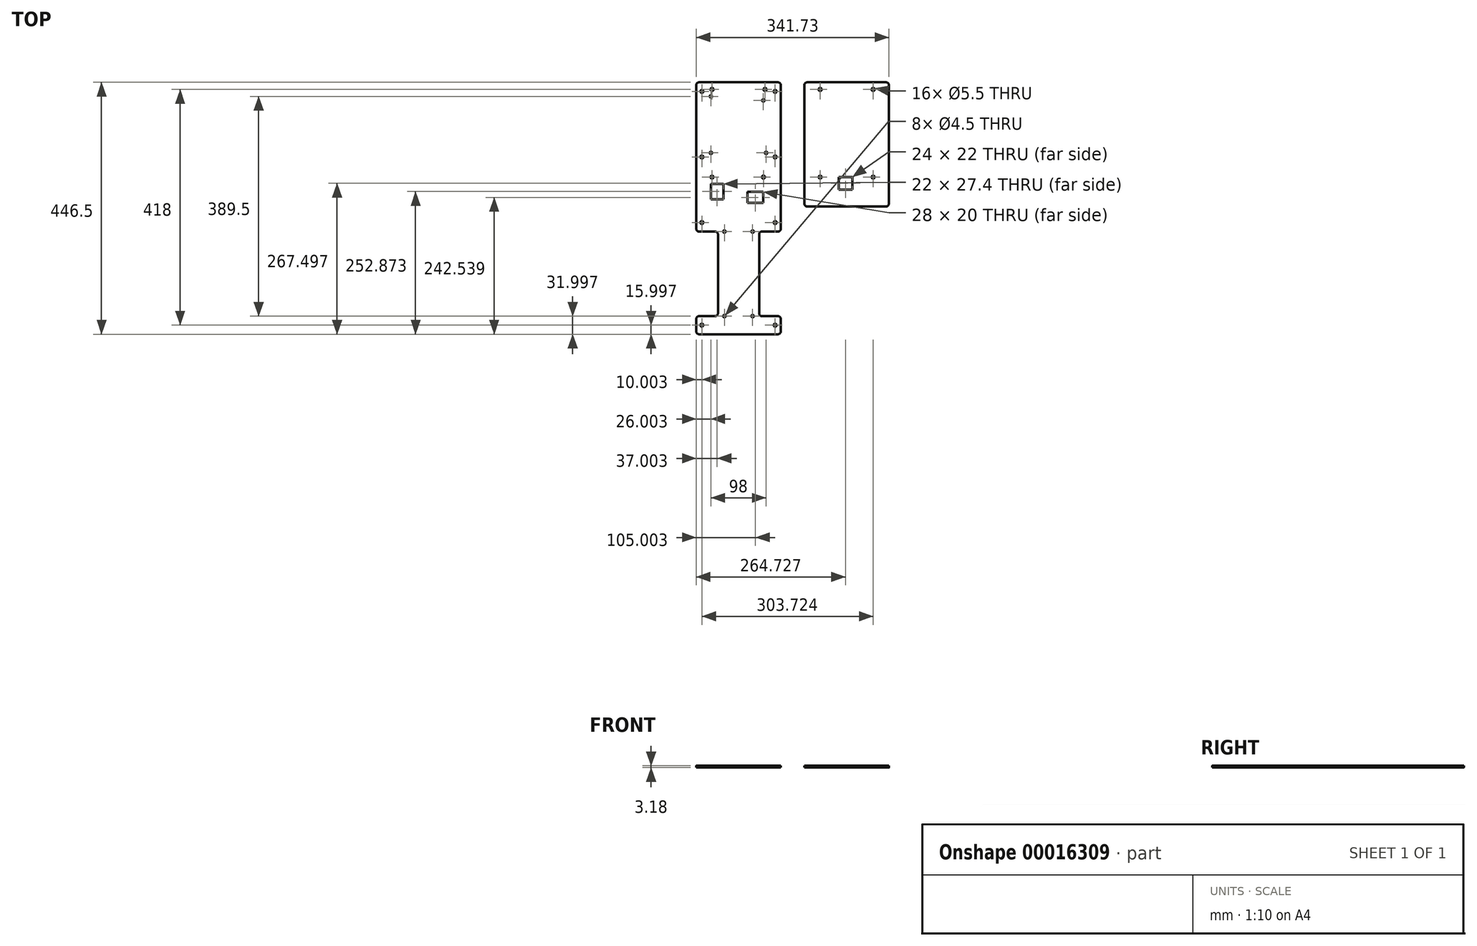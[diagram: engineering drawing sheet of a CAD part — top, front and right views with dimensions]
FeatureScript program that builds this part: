
annotation { "Feature Type Name" : "Feature", "Feature Type Description" : "" }
export const myFeature = defineFeature(function(context is Context, id is Id, definition is map)
    precondition{}
    {
        {
            var Q0;
            Q0=qCreatedBy(makeId("Top.planeOp"),FACE);
            var sketch = newSketch(context, id + "F0", { "sketchPlane" : qUnion([Q0])});
            skLineSegment(sketch, "E0.bottom", {"start": v(-64.08, 304.56) * mm, "end": v(75.92, 304.56) * mm});
            skLineSegment(sketch, "E0.top", {"start": v(-64.08, -141.94) * mm, "end": v(75.92, -141.94) * mm});
            skLineSegment(sketch, "E0.left", {"start": v(-69.08, 299.56) * mm, "end": v(-69.08, 45.06) * mm});
            skLineSegment(sketch, "E0.right", {"start": v(80.92, 299.56) * mm, "end": v(80.92, 45.06) * mm});
            skLineSegment(sketch, "E1.bottom", {"start": v(-64.08, 40.06) * mm, "end": v(-35.58, 40.06) * mm});
            skLineSegment(sketch, "E1.top", {"start": v(-64.08, -109.94) * mm, "end": v(-35.58, -109.94) * mm});
            skLineSegment(sketch, "E1.right", {"start": v(-30.58, 35.06) * mm, "end": v(-30.58, -104.94) * mm});
            skLineSegment(sketch, "E2.trimOffspring", {"start": v(-69.08, -114.94) * mm, "end": v(-69.08, -136.94) * mm});
            skLineSegment(sketch, "E3.bottom", {"start": v(75.92, 40.06) * mm, "end": v(47.42, 40.06) * mm});
            skLineSegment(sketch, "E3.top", {"start": v(75.92, -109.94) * mm, "end": v(47.42, -109.94) * mm});
            skLineSegment(sketch, "E3.right", {"start": v(42.42, 35.06) * mm, "end": v(42.42, -104.94) * mm});
            skLineSegment(sketch, "E4.trimOffspring", {"start": v(80.92, -114.94) * mm, "end": v(80.92, -136.94) * mm});
            skLineSegment(sketch, "E5", {"start": v(-69.08, -109.94) * mm, "end": v(-19.08, -109.94) * mm, "construction": true});
            skLineSegment(sketch, "E6", {"start": v(-19.08, -109.94) * mm, "end": v(30.92, -109.94) * mm, "construction": true});
            skLineSegment(sketch, "E7", {"start": v(30.92, -109.94) * mm, "end": v(80.92, -109.94) * mm, "construction": true});
            skLineSegment(sketch, "E8", {"start": v(-19.08, -109.94) * mm, "end": v(-19.08, -141.94) * mm, "construction": true});
            skLineSegment(sketch, "E9", {"start": v(-19.08, -109.94) * mm, "end": v(-19.08, 40.06) * mm, "construction": true});
            skLineSegment(sketch, "E10", {"start": v(-19.08, 40.06) * mm, "end": v(30.92, 40.06) * mm, "construction": true});
            skLineSegment(sketch, "E11", {"start": v(-19.08, 40.06) * mm, "end": v(-19.08, 72.06) * mm, "construction": true});
            skLineSegment(sketch, "E12", {"start": v(-69.08, -109.94) * mm, "end": v(-59.08, -109.94) * mm, "construction": true});
            skLineSegment(sketch, "E13", {"start": v(-59.08, -109.94) * mm, "end": v(-59.08, -125.94) * mm, "construction": true});
            skLineSegment(sketch, "E14", {"start": v(-59.08, -125.94) * mm, "end": v(-59.08, -141.94) * mm, "construction": true});
            skLineSegment(sketch, "E15", {"start": v(-69.08, -125.94) * mm, "end": v(-59.08, -125.94) * mm, "construction": true});
            skLineSegment(sketch, "E16", {"start": v(-59.08, 40.06) * mm, "end": v(-59.08, 56.06) * mm, "construction": true});
            skLineSegment(sketch, "E17", {"start": v(-59.08, 56.06) * mm, "end": v(-69.08, 56.06) * mm, "construction": true});
            skLineSegment(sketch, "E18", {"start": v(5.92, 304.56) * mm, "end": v(5.92, -141.94) * mm, "construction": true});
            skCircle(sketch, "E19", {"center": v(-59.08, -125.94) * mm, "radius": 2.75 * mm});
            skCircle(sketch, "E20", {"center": v(-59.08, 56.06) * mm, "radius": 2.75 * mm});
            skCircle(sketch, "E21", {"center": v(70.92, 56.06) * mm, "radius": 2.75 * mm});
            skCircle(sketch, "E22", {"center": v(70.92, -125.94) * mm, "radius": 2.75 * mm});
            skCircle(sketch, "E23", {"center": v(-19.08, 40.06) * mm, "radius": 2.25 * mm});
            skCircle(sketch, "E24", {"center": v(30.92, 40.06) * mm, "radius": 2.25 * mm});
            skCircle(sketch, "E25", {"center": v(-19.08, -109.94) * mm, "radius": 2.25 * mm});
            skCircle(sketch, "E26", {"center": v(30.92, -109.94) * mm, "radius": 2.25 * mm});
            skLineSegment(sketch, "E27.bottom", {"start": v(-46.58, 152.06) * mm, "end": v(58.42, 152.06) * mm, "construction": true});
            skLineSegment(sketch, "E27.top", {"start": v(-46.58, 282.06) * mm, "end": v(58.42, 282.06) * mm, "construction": true});
            skLineSegment(sketch, "E27.left", {"start": v(-46.58, 152.06) * mm, "end": v(-46.58, 282.06) * mm, "construction": true});
            skLineSegment(sketch, "E27.right", {"start": v(58.42, 152.06) * mm, "end": v(58.42, 282.06) * mm, "construction": true});
            skLineSegment(sketch, "E28", {"start": v(5.92, 72.06) * mm, "end": v(5.92, 152.06) * mm, "construction": true});
            skLineSegment(sketch, "E29", {"start": v(-46.58, 279.56) * mm, "end": v(-43.08, 279.56) * mm, "construction": true});
            skLineSegment(sketch, "E30", {"start": v(-43.08, 279.56) * mm, "end": v(-43.08, 282.06) * mm, "construction": true});
            skLineSegment(sketch, "E31", {"start": v(-46.58, 179.56) * mm, "end": v(-43.08, 179.56) * mm, "construction": true});
            skLineSegment(sketch, "E32", {"start": v(-43.08, 179.56) * mm, "end": v(-43.08, 152.06) * mm, "construction": true});
            skLineSegment(sketch, "E33", {"start": v(54.92, 152.06) * mm, "end": v(54.92, 179.56) * mm, "construction": true});
            skLineSegment(sketch, "E34", {"start": v(54.92, 179.56) * mm, "end": v(58.42, 179.56) * mm, "construction": true});
            skLineSegment(sketch, "E35", {"start": v(58.42, 272.56) * mm, "end": v(49.92, 272.56) * mm, "construction": true});
            skLineSegment(sketch, "E36", {"start": v(49.92, 272.56) * mm, "end": v(49.92, 282.06) * mm, "construction": true});
            skCircle(sketch, "E37", {"center": v(-43.08, 279.56) * mm, "radius": 2.25 * mm});
            skCircle(sketch, "E38", {"center": v(49.92, 272.56) * mm, "radius": 2.25 * mm});
            skCircle(sketch, "E39", {"center": v(-43.08, 179.56) * mm, "radius": 2.25 * mm});
            skCircle(sketch, "E40", {"center": v(54.92, 179.56) * mm, "radius": 2.25 * mm});
            skLineSegment(sketch, "E41", {"start": v(-59.03, 304.56) * mm, "end": v(-59.03, 288.56) * mm, "construction": true});
            skLineSegment(sketch, "E42", {"start": v(-59.03, 288.56) * mm, "end": v(-69.08, 288.56) * mm, "construction": true});
            skLineSegment(sketch, "E43", {"start": v(-59.03, 288.56) * mm, "end": v(-59.03, 172.3) * mm, "construction": true});
            skLineSegment(sketch, "E44", {"start": v(-59.03, 172.3) * mm, "end": v(-59.08, 56.06) * mm, "construction": true});
            skCircle(sketch, "E45", {"center": v(-59.03, 288.56) * mm, "radius": 2.75 * mm});
            skCircle(sketch, "E46", {"center": v(-59.03, 172.3) * mm, "radius": 2.75 * mm});
            skCircle(sketch, "E47", {"center": v(70.88, 288.56) * mm, "radius": 2.75 * mm});
            skCircle(sketch, "E48", {"center": v(70.88, 172.3) * mm, "radius": 2.75 * mm});
            skLineSegment(sketch, "E49", {"start": v(-46.58, 257.75) * mm, "end": v(-69.08, 257.75) * mm, "construction": true});
            skLineSegment(sketch, "E50", {"start": v(-5.88, 282.06) * mm, "end": v(-5.88, 304.56) * mm, "construction": true});
            skLineSegment(sketch, "E51.bottom", {"start": v(-43.08, 124.63) * mm, "end": v(-21.08, 124.63) * mm});
            skLineSegment(sketch, "E51.top", {"start": v(-43.08, 97.23) * mm, "end": v(-21.08, 97.23) * mm});
            skLineSegment(sketch, "E51.left", {"start": v(-43.08, 124.63) * mm, "end": v(-43.08, 97.23) * mm});
            skLineSegment(sketch, "E51.right", {"start": v(-21.08, 124.63) * mm, "end": v(-21.08, 97.23) * mm});
            skLineSegment(sketch, "E52.bottom", {"start": v(21.92, 110.6) * mm, "end": v(49.92, 110.6) * mm});
            skLineSegment(sketch, "E52.top", {"start": v(21.92, 90.6) * mm, "end": v(49.92, 90.6) * mm});
            skLineSegment(sketch, "E52.right", {"start": v(49.92, 110.6) * mm, "end": v(49.92, 90.6) * mm});
            skLineSegment(sketch, "E53", {"start": v(-21.08, 110.93) * mm, "end": v(5.92, 110.93) * mm, "construction": true});
            skLineSegment(sketch, "E54", {"start": v(80.92, 132.25) * mm, "end": v(60.92, 132.25) * mm, "construction": true});
            skLineSegment(sketch, "E55", {"start": v(21.92, 110.6) * mm, "end": v(21.92, 90.6) * mm});
            skLineSegment(sketch, "E56.bottom", {"start": v(127.65, 304.56) * mm, "end": v(267.65, 304.56) * mm});
            skLineSegment(sketch, "E56.top", {"start": v(127.65, 84.56) * mm, "end": v(267.65, 84.56) * mm});
            skLineSegment(sketch, "E56.left", {"start": v(122.65, 299.56) * mm, "end": v(122.65, 89.56) * mm});
            skLineSegment(sketch, "E56.right", {"start": v(272.65, 299.56) * mm, "end": v(272.65, 89.56) * mm});
            skLineSegment(sketch, "E57", {"start": v(36.88, 304.56) * mm, "end": v(36.88, 90.6) * mm, "construction": true});
            skLineSegment(sketch, "E58", {"start": v(-69.08, 292.06) * mm, "end": v(-41.08, 292.06) * mm, "construction": true});
            skLineSegment(sketch, "E59", {"start": v(-41.08, 292.06) * mm, "end": v(-41.08, 304.56) * mm, "construction": true});
            skLineSegment(sketch, "E60", {"start": v(80.92, 292.06) * mm, "end": v(52.92, 292.06) * mm, "construction": true});
            skLineSegment(sketch, "E61", {"start": v(52.92, 292.06) * mm, "end": v(52.92, 304.56) * mm, "construction": true});
            skLineSegment(sketch, "E62", {"start": v(122.65, 292.06) * mm, "end": v(150.65, 292.06) * mm, "construction": true});
            skLineSegment(sketch, "E63", {"start": v(150.65, 292.06) * mm, "end": v(150.65, 304.56) * mm, "construction": true});
            skLineSegment(sketch, "E64", {"start": v(272.65, 292.06) * mm, "end": v(244.65, 292.06) * mm, "construction": true});
            skLineSegment(sketch, "E65", {"start": v(244.65, 292.06) * mm, "end": v(244.65, 304.56) * mm, "construction": true});
            skLineSegment(sketch, "E66", {"start": v(122.65, 136.56) * mm, "end": v(150.65, 136.56) * mm, "construction": true});
            skLineSegment(sketch, "E67", {"start": v(150.65, 136.56) * mm, "end": v(150.65, 84.56) * mm, "construction": true});
            skLineSegment(sketch, "E68", {"start": v(244.65, 84.56) * mm, "end": v(244.65, 136.56) * mm, "construction": true});
            skLineSegment(sketch, "E69", {"start": v(244.65, 136.56) * mm, "end": v(272.65, 136.56) * mm, "construction": true});
            skLineSegment(sketch, "E70", {"start": v(-69.08, 136.56) * mm, "end": v(-41.08, 136.56) * mm, "construction": true});
            skLineSegment(sketch, "E71", {"start": v(78.17, 136.56) * mm, "end": v(50.17, 136.56) * mm, "construction": true});
            skCircle(sketch, "E72", {"center": v(-41.08, 292.06) * mm, "radius": 2.75 * mm});
            skCircle(sketch, "E73", {"center": v(52.92, 292.06) * mm, "radius": 2.75 * mm});
            skCircle(sketch, "E74", {"center": v(150.65, 292.06) * mm, "radius": 2.75 * mm});
            skCircle(sketch, "E75", {"center": v(244.65, 292.06) * mm, "radius": 2.75 * mm});
            skCircle(sketch, "E76", {"center": v(244.65, 136.56) * mm, "radius": 2.75 * mm});
            skCircle(sketch, "E77", {"center": v(150.65, 136.56) * mm, "radius": 2.75 * mm});
            skCircle(sketch, "E78", {"center": v(50.17, 136.56) * mm, "radius": 2.75 * mm});
            skCircle(sketch, "E79", {"center": v(-41.08, 136.56) * mm, "radius": 2.75 * mm});
            skPoint(sketch, "E80.visualSharp", {"position": v(122.65, 304.56) * mm});
            skArc(sketch, "E80.filletArc", {"start": v(127.65, 304.56) * mm, "mid": v(124.11, 303.1) * mm, "end": v(122.65, 299.56) * mm});
            skPoint(sketch, "E81.visualSharp", {"position": v(272.65, 304.56) * mm});
            skArc(sketch, "E81.filletArc", {"start": v(272.65, 299.56) * mm, "mid": v(271.18, 303.1) * mm, "end": v(267.65, 304.56) * mm});
            skPoint(sketch, "E82.visualSharp", {"position": v(272.65, 84.56) * mm});
            skArc(sketch, "E82.filletArc", {"start": v(267.65, 84.56) * mm, "mid": v(271.18, 86.02) * mm, "end": v(272.65, 89.56) * mm});
            skPoint(sketch, "E83.visualSharp", {"position": v(122.65, 84.56) * mm});
            skArc(sketch, "E83.filletArc", {"start": v(122.65, 89.56) * mm, "mid": v(124.11, 86.02) * mm, "end": v(127.65, 84.56) * mm});
            skPoint(sketch, "E84.visualSharp", {"position": v(-69.08, 304.56) * mm});
            skArc(sketch, "E84.filletArc", {"start": v(-64.08, 304.56) * mm, "mid": v(-67.61, 303.1) * mm, "end": v(-69.08, 299.56) * mm});
            skPoint(sketch, "E85.visualSharp", {"position": v(80.92, 304.56) * mm});
            skArc(sketch, "E85.filletArc", {"start": v(80.92, 299.56) * mm, "mid": v(79.46, 303.1) * mm, "end": v(75.92, 304.56) * mm});
            skPoint(sketch, "E86.visualSharp", {"position": v(80.92, 40.06) * mm});
            skArc(sketch, "E86.filletArc", {"start": v(75.92, 40.06) * mm, "mid": v(79.46, 41.52) * mm, "end": v(80.92, 45.06) * mm});
            skPoint(sketch, "E87.visualSharp", {"position": v(42.42, 40.06) * mm});
            skArc(sketch, "E87.filletArc", {"start": v(47.42, 40.06) * mm, "mid": v(43.89, 38.6) * mm, "end": v(42.42, 35.06) * mm});
            skPoint(sketch, "E88.visualSharp", {"position": v(42.42, -109.94) * mm});
            skArc(sketch, "E88.filletArc", {"start": v(42.42, -104.94) * mm, "mid": v(43.89, -108.48) * mm, "end": v(47.42, -109.94) * mm});
            skPoint(sketch, "E89.visualSharp", {"position": v(80.92, -109.94) * mm});
            skArc(sketch, "E89.filletArc", {"start": v(80.92, -114.94) * mm, "mid": v(79.46, -111.4) * mm, "end": v(75.92, -109.94) * mm});
            skPoint(sketch, "E90.visualSharp", {"position": v(80.92, -141.94) * mm});
            skArc(sketch, "E90.filletArc", {"start": v(75.92, -141.94) * mm, "mid": v(79.46, -140.48) * mm, "end": v(80.92, -136.94) * mm});
            skPoint(sketch, "E91.visualSharp", {"position": v(-69.08, -141.94) * mm});
            skArc(sketch, "E91.filletArc", {"start": v(-69.08, -136.94) * mm, "mid": v(-67.61, -140.48) * mm, "end": v(-64.08, -141.94) * mm});
            skPoint(sketch, "E92.visualSharp", {"position": v(-69.08, -109.94) * mm});
            skArc(sketch, "E92.filletArc", {"start": v(-64.08, -109.94) * mm, "mid": v(-67.61, -111.4) * mm, "end": v(-69.08, -114.94) * mm});
            skPoint(sketch, "E93.visualSharp", {"position": v(-30.58, -109.94) * mm});
            skArc(sketch, "E93.filletArc", {"start": v(-35.58, -109.94) * mm, "mid": v(-32.04, -108.48) * mm, "end": v(-30.58, -104.94) * mm});
            skPoint(sketch, "E94.visualSharp", {"position": v(-30.58, 40.06) * mm});
            skArc(sketch, "E94.filletArc", {"start": v(-30.58, 35.06) * mm, "mid": v(-32.04, 38.6) * mm, "end": v(-35.58, 40.06) * mm});
            skPoint(sketch, "E95.visualSharp", {"position": v(-69.08, 40.06) * mm});
            skArc(sketch, "E95.filletArc", {"start": v(-69.08, 45.06) * mm, "mid": v(-67.61, 41.52) * mm, "end": v(-64.08, 40.06) * mm});
            skLineSegment(sketch, "E96.bottom", {"start": v(183.65, 136.56) * mm, "end": v(207.65, 136.56) * mm});
            skLineSegment(sketch, "E96.top", {"start": v(183.65, 114.56) * mm, "end": v(207.65, 114.56) * mm});
            skLineSegment(sketch, "E96.left", {"start": v(183.65, 136.56) * mm, "end": v(183.65, 114.56) * mm});
            skLineSegment(sketch, "E96.right", {"start": v(207.65, 136.56) * mm, "end": v(207.65, 114.56) * mm});
            skLineSegment(sketch, "E97", {"start": v(195.65, 114.56) * mm, "end": v(195.65, 84.56) * mm, "construction": true});
            skLineSegment(sketch, "E98", {"start": v(207.65, 125.56) * mm, "end": v(272.65, 125.56) * mm, "construction": true});
            skLineSegment(sketch, "E99", {"start": v(195.65, 84.56) * mm, "end": v(195.65, 304.56) * mm, "construction": true});
            skSolve(sketch);
        }
        {
            var Q0;
            Q0=makeQuery(id+"F0.imprint","IMPRINT",FACE,{"disambiguationData":[TD([[makeQuery(id+"F0.imprint","IMPRINT",EDGE,{"derivedFrom":sQuery(id+"F0.wireOp",EDGE,"E0.bottom")}),-1.0]])]});
            extrude(context, id + "F1", {"entities" : qUnion([Q0]), "depth" : 3.17 * mm});
        }
        {
            var Q0;
            Q0=makeQuery(id+"F0.imprint","IMPRINT",FACE,{"disambiguationData":[TD([[makeQuery(id+"F0.imprint","IMPRINT",EDGE,{"derivedFrom":sQuery(id+"F0.wireOp",EDGE,"E56.bottom")}),-1.0]])]});
            extrude(context, id + "F2", {"entities" : qUnion([Q0]), "depth" : 3.17 * mm});
        }
    });
